# Revit family: 240341WCG01-013-WCE97US6K_240341WCG01-013-WCE97US6KS
name_source: partatom
category: Specialty Equipment
units: mm (PartAtom-declared; Revit-internal decimal feet)

## family parameters
Always vertical = Yes
Cut with Voids When Loaded = No
Enable Cutting in Views = No
Maintain Annotation Orientation = No
Part Type = Normal
Room Calculation Point = No
Round Connector Dimension = Use Diameter
Shared = No
Work Plane-Based = No

## types (1)
- WCE97US6KS
    Amps = 40 A
    Body Material = ARCAT - Metal - Aluminum
    Default Elevation = 0 "
    Depth = 22.81 "
    Description = 36-inch Electric Ceramic Glass Cooktop with Triple Radiant Element
    Energy Guide = https://www.whirlpool.com
    Family Name = Loki
    Feature 1 = FlexHeat™ Triple Radiant Element
    Feature 2 = Tap Touch Controls
    Feature 3 = Control Lock Mode
    Height = 5.25 "
    Installation-Fabrication = https://www.whirlpool.com
    Ring Material = ARCAT - Metal - Aluminum(1)
    Top Panel Material = ARCAT - Metal - Gray
    Voltage = 240 V
    Width = 36.31 "

## geometry (parser evidence)
native form markers: Sweep x38
no freeform markers — native parametric forms only
